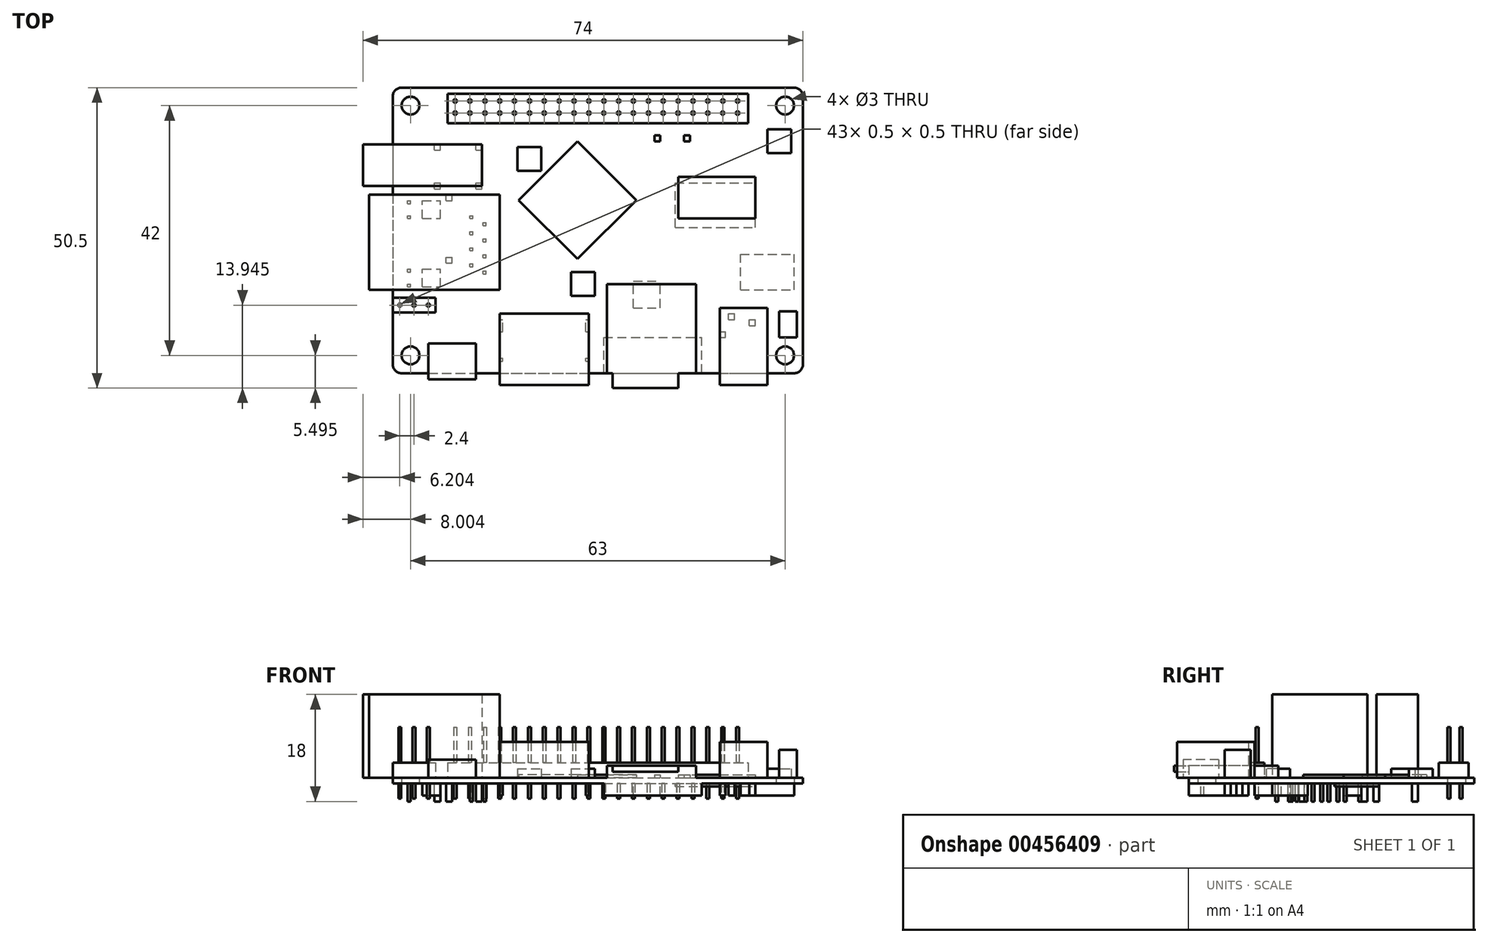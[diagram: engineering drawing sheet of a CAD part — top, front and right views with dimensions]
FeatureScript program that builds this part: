
annotation { "Feature Type Name" : "Feature", "Feature Type Description" : "" }
export const myFeature = defineFeature(function(context is Context, id is Id, definition is map)
    precondition{}
    {
        {
            var Q0;
            Q0=qCreatedBy(makeId("Top.planeOp"),FACE);
            var sketch = newSketch(context, id + "F0", { "sketchPlane" : qUnion([Q0])});
            skLineSegment(sketch, "E0.bottom", {"start": v(-42.34, 28.44) * mm, "end": v(23.66, 28.44) * mm});
            skLineSegment(sketch, "E0.top", {"start": v(-42.34, -19.56) * mm, "end": v(23.66, -19.56) * mm});
            skLineSegment(sketch, "E0.left", {"start": v(-43.84, 26.94) * mm, "end": v(-43.84, -18.06) * mm});
            skLineSegment(sketch, "E0.right", {"start": v(25.16, 26.94) * mm, "end": v(25.16, -18.06) * mm});
            skPoint(sketch, "E1", {"position": v(-43.84, 28.44) * mm});
            skCircle(sketch, "E2", {"center": v(-40.84, 25.44) * mm, "radius": 1.5 * mm});
            skCircle(sketch, "E3", {"center": v(22.16, 25.44) * mm, "radius": 1.5 * mm});
            skCircle(sketch, "E4", {"center": v(22.16, -16.56) * mm, "radius": 1.5 * mm});
            skCircle(sketch, "E5", {"center": v(-40.84, -16.56) * mm, "radius": 1.5 * mm});
            skLineSegment(sketch, "E6.bottom", {"start": v(-37.84, -19.56) * mm, "end": v(19.16, -19.56) * mm});
            skPoint(sketch, "E7.visualSharp", {"position": v(25.16, 28.44) * mm});
            skArc(sketch, "E7.filletArc", {"start": v(25.16, 26.94) * mm, "mid": v(24.72, 28) * mm, "end": v(23.66, 28.44) * mm});
            skArc(sketch, "E8.filletArc", {"start": v(-42.34, 28.44) * mm, "mid": v(-43.4, 28) * mm, "end": v(-43.84, 26.94) * mm});
            skPoint(sketch, "E9.visualSharp", {"position": v(-43.84, -19.56) * mm});
            skArc(sketch, "E9.filletArc", {"start": v(-43.84, -18.06) * mm, "mid": v(-43.4, -19.13) * mm, "end": v(-42.34, -19.56) * mm});
            skPoint(sketch, "E10.visualSharp", {"position": v(25.16, -19.56) * mm});
            skArc(sketch, "E10.filletArc", {"start": v(23.66, -19.56) * mm, "mid": v(24.72, -19.13) * mm, "end": v(25.16, -18.06) * mm});
            skSolve(sketch);
        }
        {
            var Q0;
            Q0=makeQuery(id+"F0.imprint","IMPRINT",FACE,{"disambiguationData":[TD([[makeQuery(id+"F0.imprint","IMPRINT",EDGE,{"derivedFrom":sQuery(id+"F0.wireOp",EDGE,"E0.bottom")}),-1.0]])]});
            extrude(context, id + "F1", {"entities" : qUnion([Q0]), "depth" : 1 * mm});
        }
        {
            var Q0;
            Q0=makeQuery(id+"F1.opExtrude","CAP_FACE",FACE,{"disambiguationData":[OSD([sQuery(id+"F0.wireOp",EDGE,"E0.bottom"),sQuery(id+"F0.wireOp",EDGE,"E0.top"),sQuery(id+"F0.wireOp",EDGE,"E0.left"),sQuery(id+"F0.wireOp",EDGE,"E0.right"),sQuery(id+"F0.wireOp",EDGE,"E2"),sQuery(id+"F0.wireOp",EDGE,"E3"),sQuery(id+"F0.wireOp",EDGE,"E4"),sQuery(id+"F0.wireOp",EDGE,"E5"),sQuery(id+"F0.wireOp",EDGE,"E6.bottom"),sQuery(id+"F0.wireOp",EDGE,"E7.filletArc"),sQuery(id+"F0.wireOp",EDGE,"E8.filletArc"),sQuery(id+"F0.wireOp",EDGE,"E9.filletArc"),sQuery(id+"F0.wireOp",EDGE,"E10.filletArc")])],"isStart":false});
            var sketch = newSketch(context, id + "F2", { "sketchPlane" : qUnion([Q0])});
            skLineSegment(sketch, "E11.bottom", {"start": v(24.16, -13.56) * mm, "end": v(21.16, -13.56) * mm});
            skLineSegment(sketch, "E11.top", {"start": v(24.16, -9.16) * mm, "end": v(21.16, -9.16) * mm});
            skLineSegment(sketch, "E11.left", {"start": v(24.16, -13.56) * mm, "end": v(24.16, -9.16) * mm});
            skLineSegment(sketch, "E11.right", {"start": v(21.16, -13.56) * mm, "end": v(21.16, -9.16) * mm});
            skSolve(sketch);
        }
        {
            var Q0;
            Q0=makeQuery(id+"F2.imprint","IMPRINT",FACE,{"disambiguationData":[TD([[makeQuery(id+"F2.imprint","IMPRINT",EDGE,{"derivedFrom":sQuery(id+"F2.wireOp",EDGE,"E11.bottom")}),-1.0]])]});
            extrude(context, id + "F3", {"entities" : qUnion([Q0]), "operationType" : NewBodyOperationType.ADD, "depth" : 4.7 * mm});
        }
        {
            var Q0;
            Q0=makeQuery(id+"F3.opExtrude","SWEPT_FACE",FACE,{"disambiguationData":[OSD([sQuery(id+"F2.wireOp",EDGE,"E11.left")])]});
            var sketch = newSketch(context, id + "F4", { "sketchPlane" : qUnion([Q0])});
            skCircle(sketch, "E12", {"center": v(-11.39, 3.44) * mm, "radius": 1.05 * mm});
            skSolve(sketch);
        }
        {
            var Q0;
            Q0=sQuery(id+"F4.wireOp",EDGE,"E12");
            extrude(context, id + "F5", {"bodyType" : ToolBodyType.SURFACE, "surfaceEntities" : qUnion([Q0]), "depth" : 2 * mm});
        }
        {
            var Q0;
            Q0=makeQuery(id+"F1.opExtrude","CAP_FACE",FACE,{"disambiguationData":[OSD([sQuery(id+"F0.wireOp",EDGE,"E0.bottom"),sQuery(id+"F0.wireOp",EDGE,"E0.top"),sQuery(id+"F0.wireOp",EDGE,"E0.left"),sQuery(id+"F0.wireOp",EDGE,"E0.right"),sQuery(id+"F0.wireOp",EDGE,"E2"),sQuery(id+"F0.wireOp",EDGE,"E3"),sQuery(id+"F0.wireOp",EDGE,"E4"),sQuery(id+"F0.wireOp",EDGE,"E5"),sQuery(id+"F0.wireOp",EDGE,"E6.bottom"),sQuery(id+"F0.wireOp",EDGE,"E7.filletArc"),sQuery(id+"F0.wireOp",EDGE,"E8.filletArc"),sQuery(id+"F0.wireOp",EDGE,"E9.filletArc"),sQuery(id+"F0.wireOp",EDGE,"E10.filletArc")])],"isStart":false});
            var sketch = newSketch(context, id + "F6", { "sketchPlane" : qUnion([Q0])});
            skLineSegment(sketch, "E13.bottom", {"start": v(11.16, -8.56) * mm, "end": v(19.16, -8.56) * mm});
            skLineSegment(sketch, "E13.top", {"start": v(11.16, -21.56) * mm, "end": v(19.16, -21.56) * mm});
            skLineSegment(sketch, "E13.left", {"start": v(11.16, -8.56) * mm, "end": v(11.16, -21.56) * mm});
            skLineSegment(sketch, "E13.right", {"start": v(19.16, -8.56) * mm, "end": v(19.16, -21.56) * mm});
            skSolve(sketch);
        }
        {
            var Q0;
            Q0 = qSketchRegion(id + "F6", true);
            extrude(context, id + "F7", {"entities" : qUnion([Q0]), "operationType" : NewBodyOperationType.ADD, "depth" : 6 * mm});
        }
        {
            var Q0;
            Q0=makeQuery(id+"F1.opExtrude","CAP_FACE",FACE,{"disambiguationData":[OSD([sQuery(id+"F0.wireOp",EDGE,"E0.bottom"),sQuery(id+"F0.wireOp",EDGE,"E0.top"),sQuery(id+"F0.wireOp",EDGE,"E0.left"),sQuery(id+"F0.wireOp",EDGE,"E0.right"),sQuery(id+"F0.wireOp",EDGE,"E2"),sQuery(id+"F0.wireOp",EDGE,"E3"),sQuery(id+"F0.wireOp",EDGE,"E4"),sQuery(id+"F0.wireOp",EDGE,"E5"),sQuery(id+"F0.wireOp",EDGE,"E6.bottom"),sQuery(id+"F0.wireOp",EDGE,"E7.filletArc"),sQuery(id+"F0.wireOp",EDGE,"E8.filletArc"),sQuery(id+"F0.wireOp",EDGE,"E9.filletArc"),sQuery(id+"F0.wireOp",EDGE,"E10.filletArc")])],"isStart":false});
            var sketch = newSketch(context, id + "F8", { "sketchPlane" : qUnion([Q0])});
            skLineSegment(sketch, "E14.bottom", {"start": v(-7.84, -4.56) * mm, "end": v(7.16, -4.56) * mm});
            skLineSegment(sketch, "E14.top", {"start": v(-7.84, -19.56) * mm, "end": v(7.16, -19.56) * mm});
            skLineSegment(sketch, "E14.left", {"start": v(-7.84, -4.56) * mm, "end": v(-7.84, -19.56) * mm});
            skLineSegment(sketch, "E14.right", {"start": v(7.16, -4.56) * mm, "end": v(7.16, -19.56) * mm});
            skSolve(sketch);
        }
        {
            var Q0;
            Q0 = qSketchRegion(id + "F8", true);
            extrude(context, id + "F9", {"entities" : qUnion([Q0]), "operationType" : NewBodyOperationType.ADD, "depth" : 2 * mm});
        }
        {
            var Q0;
            Q0=makeQuery(id+"F9.boolean.opBoolean","MERGE",FACE,{"derivedFrom":[makeQuery(id+"F1.opExtrude","SWEPT_FACE",FACE,{"disambiguationData":[OSD([sQuery(id+"F0.wireOp",EDGE,"E0.top"),sQuery(id+"F0.wireOp",EDGE,"E6.bottom")])]}),makeQuery(id+"F9.opExtrude","SWEPT_FACE",FACE,{"disambiguationData":[OSD([sQuery(id+"F8.wireOp",EDGE,"E14.top")])]})]});
            var sketch = newSketch(context, id + "F10", { "sketchPlane" : qUnion([Q0])});
            skLineSegment(sketch, "E15.bottom", {"start": v(-6.84, 3) * mm, "end": v(4.16, 3) * mm});
            skLineSegment(sketch, "E15.top", {"start": v(-6.84, 2) * mm, "end": v(4.16, 2) * mm});
            skLineSegment(sketch, "E15.left", {"start": v(-6.84, 3) * mm, "end": v(-6.84, 2) * mm});
            skLineSegment(sketch, "E15.right", {"start": v(4.16, 3) * mm, "end": v(4.16, 2) * mm});
            skSolve(sketch);
        }
        {
            var Q0;
            Q0 = qSketchRegion(id + "F10", true);
            extrude(context, id + "F11", {"entities" : qUnion([Q0]), "operationType" : NewBodyOperationType.ADD, "depth" : 2.5 * mm});
        }
        {
            var Q0;
            Q0=makeQuery(id+"F1.opExtrude","CAP_FACE",FACE,{"disambiguationData":[OSD([sQuery(id+"F0.wireOp",EDGE,"E0.bottom"),sQuery(id+"F0.wireOp",EDGE,"E0.top"),sQuery(id+"F0.wireOp",EDGE,"E0.left"),sQuery(id+"F0.wireOp",EDGE,"E0.right"),sQuery(id+"F0.wireOp",EDGE,"E2"),sQuery(id+"F0.wireOp",EDGE,"E3"),sQuery(id+"F0.wireOp",EDGE,"E4"),sQuery(id+"F0.wireOp",EDGE,"E5"),sQuery(id+"F0.wireOp",EDGE,"E6.bottom"),sQuery(id+"F0.wireOp",EDGE,"E7.filletArc"),sQuery(id+"F0.wireOp",EDGE,"E8.filletArc"),sQuery(id+"F0.wireOp",EDGE,"E9.filletArc"),sQuery(id+"F0.wireOp",EDGE,"E10.filletArc")])],"isStart":false});
            var sketch = newSketch(context, id + "F12", { "sketchPlane" : qUnion([Q0])});
            skLineSegment(sketch, "E16.bottom", {"start": v(-25.84, -9.56) * mm, "end": v(-10.84, -9.56) * mm});
            skLineSegment(sketch, "E16.top", {"start": v(-25.84, -21.56) * mm, "end": v(-10.84, -21.56) * mm});
            skLineSegment(sketch, "E16.left", {"start": v(-25.84, -9.56) * mm, "end": v(-25.84, -21.56) * mm});
            skLineSegment(sketch, "E16.right", {"start": v(-10.84, -9.56) * mm, "end": v(-10.84, -21.56) * mm});
            skSolve(sketch);
        }
        {
            var Q0;
            Q0 = qSketchRegion(id + "F12", true);
            extrude(context, id + "F13", {"entities" : qUnion([Q0]), "operationType" : NewBodyOperationType.ADD, "depth" : 6 * mm});
        }
        {
            var Q0;
            Q0=makeQuery(id+"F1.opExtrude","CAP_FACE",FACE,{"disambiguationData":[OSD([sQuery(id+"F0.wireOp",EDGE,"E0.bottom"),sQuery(id+"F0.wireOp",EDGE,"E0.top"),sQuery(id+"F0.wireOp",EDGE,"E0.left"),sQuery(id+"F0.wireOp",EDGE,"E0.right"),sQuery(id+"F0.wireOp",EDGE,"E2"),sQuery(id+"F0.wireOp",EDGE,"E3"),sQuery(id+"F0.wireOp",EDGE,"E4"),sQuery(id+"F0.wireOp",EDGE,"E5"),sQuery(id+"F0.wireOp",EDGE,"E6.bottom"),sQuery(id+"F0.wireOp",EDGE,"E7.filletArc"),sQuery(id+"F0.wireOp",EDGE,"E8.filletArc"),sQuery(id+"F0.wireOp",EDGE,"E9.filletArc"),sQuery(id+"F0.wireOp",EDGE,"E10.filletArc")])],"isStart":false});
            var sketch = newSketch(context, id + "F14", { "sketchPlane" : qUnion([Q0])});
            skLineSegment(sketch, "E17.bottom", {"start": v(-37.84, -14.56) * mm, "end": v(-29.84, -14.56) * mm});
            skLineSegment(sketch, "E17.top", {"start": v(-37.84, -20.56) * mm, "end": v(-29.84, -20.56) * mm});
            skLineSegment(sketch, "E17.left", {"start": v(-37.84, -14.56) * mm, "end": v(-37.84, -20.56) * mm});
            skLineSegment(sketch, "E17.right", {"start": v(-29.84, -14.56) * mm, "end": v(-29.84, -20.56) * mm});
            skSolve(sketch);
        }
        {
            var Q0;
            Q0 = qSketchRegion(id + "F14", true);
            extrude(context, id + "F15", {"entities" : qUnion([Q0]), "operationType" : NewBodyOperationType.ADD, "depth" : 3 * mm});
        }
        {
            var Q0;
            Q0=makeQuery(id+"F1.opExtrude","CAP_FACE",FACE,{"disambiguationData":[OSD([sQuery(id+"F0.wireOp",EDGE,"E0.bottom"),sQuery(id+"F0.wireOp",EDGE,"E0.top"),sQuery(id+"F0.wireOp",EDGE,"E0.left"),sQuery(id+"F0.wireOp",EDGE,"E0.right"),sQuery(id+"F0.wireOp",EDGE,"E2"),sQuery(id+"F0.wireOp",EDGE,"E3"),sQuery(id+"F0.wireOp",EDGE,"E4"),sQuery(id+"F0.wireOp",EDGE,"E5"),sQuery(id+"F0.wireOp",EDGE,"E6.bottom"),sQuery(id+"F0.wireOp",EDGE,"E7.filletArc"),sQuery(id+"F0.wireOp",EDGE,"E8.filletArc"),sQuery(id+"F0.wireOp",EDGE,"E9.filletArc"),sQuery(id+"F0.wireOp",EDGE,"E10.filletArc")])],"isStart":false});
            var sketch = newSketch(context, id + "F16", { "sketchPlane" : qUnion([Q0])});
            skLineSegment(sketch, "E18.bottom", {"start": v(-43.84, -6.86) * mm, "end": v(-36.64, -6.86) * mm});
            skLineSegment(sketch, "E18.top", {"start": v(-43.84, -9.36) * mm, "end": v(-36.64, -9.36) * mm});
            skLineSegment(sketch, "E18.left", {"start": v(-43.84, -6.86) * mm, "end": v(-43.84, -9.36) * mm});
            skLineSegment(sketch, "E18.right", {"start": v(-36.64, -6.86) * mm, "end": v(-36.64, -9.36) * mm});
            skSolve(sketch);
        }
        {
            var Q0;
            Q0 = qSketchRegion(id + "F16", true);
            extrude(context, id + "F17", {"entities" : qUnion([Q0]), "operationType" : NewBodyOperationType.ADD, "depth" : 2.5 * mm});
        }
        {
            var Q0;
            Q0=makeQuery(id+"F17.opExtrude","CAP_FACE",FACE,{"disambiguationData":[OSD([sQuery(id+"F16.wireOp",EDGE,"E18.bottom"),sQuery(id+"F16.wireOp",EDGE,"E18.top"),sQuery(id+"F16.wireOp",EDGE,"E18.left"),sQuery(id+"F16.wireOp",EDGE,"E18.right")])],"isStart":false});
            var sketch = newSketch(context, id + "F18", { "sketchPlane" : qUnion([Q0])});
            skLineSegment(sketch, "E19.bottom", {"start": v(-42.89, -7.86) * mm, "end": v(-42.39, -7.86) * mm});
            skLineSegment(sketch, "E19.top", {"start": v(-42.89, -8.36) * mm, "end": v(-42.39, -8.36) * mm});
            skLineSegment(sketch, "E19.left", {"start": v(-42.89, -7.86) * mm, "end": v(-42.89, -8.36) * mm});
            skLineSegment(sketch, "E19.right", {"start": v(-42.39, -7.86) * mm, "end": v(-42.39, -8.36) * mm});
            skLineSegment(sketch, "E20.bottom", {"start": v(-40.49, -7.86) * mm, "end": v(-39.99, -7.86) * mm});
            skLineSegment(sketch, "E20.top", {"start": v(-40.49, -8.36) * mm, "end": v(-39.99, -8.36) * mm});
            skLineSegment(sketch, "E20.left", {"start": v(-40.49, -7.86) * mm, "end": v(-40.49, -8.36) * mm});
            skLineSegment(sketch, "E20.right", {"start": v(-39.99, -7.86) * mm, "end": v(-39.99, -8.36) * mm});
            skLineSegment(sketch, "E21.bottom", {"start": v(-38.09, -7.86) * mm, "end": v(-37.59, -7.86) * mm});
            skLineSegment(sketch, "E21.top", {"start": v(-38.09, -8.36) * mm, "end": v(-37.59, -8.36) * mm});
            skLineSegment(sketch, "E21.left", {"start": v(-38.09, -7.86) * mm, "end": v(-38.09, -8.36) * mm});
            skLineSegment(sketch, "E21.right", {"start": v(-37.59, -7.86) * mm, "end": v(-37.59, -8.36) * mm});
            skSolve(sketch);
        }
        {
            var Q0;
            Q0 = qSketchRegion(id + "F18", true);
            extrude(context, id + "F19", {"entities" : qUnion([Q0]), "operationType" : NewBodyOperationType.ADD, "depth" : 6 * mm});
        }
        {
            var Q0;
            Q0=makeQuery(id+"F1.opExtrude","CAP_FACE",FACE,{"disambiguationData":[OSD([sQuery(id+"F0.wireOp",EDGE,"E0.bottom"),sQuery(id+"F0.wireOp",EDGE,"E0.top"),sQuery(id+"F0.wireOp",EDGE,"E0.left"),sQuery(id+"F0.wireOp",EDGE,"E0.right"),sQuery(id+"F0.wireOp",EDGE,"E2"),sQuery(id+"F0.wireOp",EDGE,"E3"),sQuery(id+"F0.wireOp",EDGE,"E4"),sQuery(id+"F0.wireOp",EDGE,"E5"),sQuery(id+"F0.wireOp",EDGE,"E6.bottom"),sQuery(id+"F0.wireOp",EDGE,"E7.filletArc"),sQuery(id+"F0.wireOp",EDGE,"E8.filletArc"),sQuery(id+"F0.wireOp",EDGE,"E9.filletArc"),sQuery(id+"F0.wireOp",EDGE,"E10.filletArc")])],"isStart":false});
            var sketch = newSketch(context, id + "F20", { "sketchPlane" : qUnion([Q0])});
            skLineSegment(sketch, "E22.bottom", {"start": v(-25.84, 10.44) * mm, "end": v(-47.84, 10.44) * mm});
            skLineSegment(sketch, "E22.top", {"start": v(-25.84, -5.56) * mm, "end": v(-47.84, -5.56) * mm});
            skLineSegment(sketch, "E22.left", {"start": v(-25.84, 10.44) * mm, "end": v(-25.84, -5.56) * mm});
            skLineSegment(sketch, "E22.right", {"start": v(-47.84, 10.44) * mm, "end": v(-47.84, -5.56) * mm});
            skSolve(sketch);
        }
        {
            var Q0;
            Q0 = qSketchRegion(id + "F20", true);
            extrude(context, id + "F21", {"entities" : qUnion([Q0]), "operationType" : NewBodyOperationType.ADD, "depth" : 14 * mm});
        }
        {
            var Q0;
            Q0=makeQuery(id+"F1.opExtrude","CAP_FACE",FACE,{"disambiguationData":[OSD([sQuery(id+"F0.wireOp",EDGE,"E0.bottom"),sQuery(id+"F0.wireOp",EDGE,"E0.top"),sQuery(id+"F0.wireOp",EDGE,"E0.left"),sQuery(id+"F0.wireOp",EDGE,"E0.right"),sQuery(id+"F0.wireOp",EDGE,"E2"),sQuery(id+"F0.wireOp",EDGE,"E3"),sQuery(id+"F0.wireOp",EDGE,"E4"),sQuery(id+"F0.wireOp",EDGE,"E5"),sQuery(id+"F0.wireOp",EDGE,"E6.bottom"),sQuery(id+"F0.wireOp",EDGE,"E7.filletArc"),sQuery(id+"F0.wireOp",EDGE,"E8.filletArc"),sQuery(id+"F0.wireOp",EDGE,"E9.filletArc"),sQuery(id+"F0.wireOp",EDGE,"E10.filletArc")])],"isStart":false});
            var sketch = newSketch(context, id + "F22", { "sketchPlane" : qUnion([Q0])});
            skLineSegment(sketch, "E23.bottom", {"start": v(-48.84, 18.94) * mm, "end": v(-28.84, 18.94) * mm});
            skLineSegment(sketch, "E23.top", {"start": v(-48.84, 11.94) * mm, "end": v(-28.84, 11.94) * mm});
            skLineSegment(sketch, "E23.left", {"start": v(-48.84, 18.94) * mm, "end": v(-48.84, 11.94) * mm});
            skLineSegment(sketch, "E23.right", {"start": v(-28.84, 18.94) * mm, "end": v(-28.84, 11.94) * mm});
            skSolve(sketch);
        }
        {
            var Q0;
            Q0 = qSketchRegion(id + "F22", true);
            extrude(context, id + "F23", {"entities" : qUnion([Q0]), "operationType" : NewBodyOperationType.ADD, "depth" : 14 * mm});
        }
        {
            var Q0;
            Q0=makeQuery(id+"F1.opExtrude","CAP_FACE",FACE,{"disambiguationData":[OSD([sQuery(id+"F0.wireOp",EDGE,"E0.bottom"),sQuery(id+"F0.wireOp",EDGE,"E0.top"),sQuery(id+"F0.wireOp",EDGE,"E0.left"),sQuery(id+"F0.wireOp",EDGE,"E0.right"),sQuery(id+"F0.wireOp",EDGE,"E2"),sQuery(id+"F0.wireOp",EDGE,"E3"),sQuery(id+"F0.wireOp",EDGE,"E4"),sQuery(id+"F0.wireOp",EDGE,"E5"),sQuery(id+"F0.wireOp",EDGE,"E6.bottom"),sQuery(id+"F0.wireOp",EDGE,"E7.filletArc"),sQuery(id+"F0.wireOp",EDGE,"E8.filletArc"),sQuery(id+"F0.wireOp",EDGE,"E9.filletArc"),sQuery(id+"F0.wireOp",EDGE,"E10.filletArc")])],"isStart":false});
            var sketch = newSketch(context, id + "F24", { "sketchPlane" : qUnion([Q0])});
            skLineSegment(sketch, "E24.bottom", {"start": v(-34.59, 27.44) * mm, "end": v(15.91, 27.44) * mm});
            skLineSegment(sketch, "E24.top", {"start": v(-34.59, 22.44) * mm, "end": v(15.91, 22.44) * mm});
            skLineSegment(sketch, "E24.left", {"start": v(-34.59, 27.44) * mm, "end": v(-34.59, 22.44) * mm});
            skLineSegment(sketch, "E24.right", {"start": v(15.91, 27.44) * mm, "end": v(15.91, 22.44) * mm});
            skSolve(sketch);
        }
        {
            var Q0;
            Q0 = qSketchRegion(id + "F24", true);
            extrude(context, id + "F25", {"entities" : qUnion([Q0]), "operationType" : NewBodyOperationType.ADD, "depth" : 2.5 * mm});
        }
        {
            var Q0;
            Q0=makeQuery(id+"F25.opExtrude","CAP_FACE",FACE,{"disambiguationData":[OSD([sQuery(id+"F24.wireOp",EDGE,"E24.bottom"),sQuery(id+"F24.wireOp",EDGE,"E24.top"),sQuery(id+"F24.wireOp",EDGE,"E24.left"),sQuery(id+"F24.wireOp",EDGE,"E24.right")])],"isStart":false});
            var sketch = newSketch(context, id + "F26", { "sketchPlane" : qUnion([Q0])});
            skLineSegment(sketch, "E25.bottom", {"start": v(-33.59, 26.44) * mm, "end": v(-33.09, 26.44) * mm});
            skLineSegment(sketch, "E25.top", {"start": v(-33.59, 25.94) * mm, "end": v(-33.09, 25.94) * mm});
            skLineSegment(sketch, "E25.left", {"start": v(-33.59, 26.44) * mm, "end": v(-33.59, 25.94) * mm});
            skLineSegment(sketch, "E25.right", {"start": v(-33.09, 26.44) * mm, "end": v(-33.09, 25.94) * mm});
            skLineSegment(sketch, "E26.1.0.0", {"start": v(-31.09, 26.44) * mm, "end": v(-31.09, 25.94) * mm});
            skLineSegment(sketch, "E26.1.0.1", {"start": v(-31.09, 26.44) * mm, "end": v(-30.59, 26.44) * mm});
            skLineSegment(sketch, "E26.1.0.2", {"start": v(-30.59, 26.44) * mm, "end": v(-30.59, 25.94) * mm});
            skLineSegment(sketch, "E26.1.0.3", {"start": v(-31.09, 25.94) * mm, "end": v(-30.59, 25.94) * mm});
            skLineSegment(sketch, "E26.2.0.0", {"start": v(-28.59, 26.44) * mm, "end": v(-28.59, 25.94) * mm});
            skLineSegment(sketch, "E26.2.0.1", {"start": v(-28.59, 26.44) * mm, "end": v(-28.09, 26.44) * mm});
            skLineSegment(sketch, "E26.2.0.2", {"start": v(-28.09, 26.44) * mm, "end": v(-28.09, 25.94) * mm});
            skLineSegment(sketch, "E26.2.0.3", {"start": v(-28.59, 25.94) * mm, "end": v(-28.09, 25.94) * mm});
            skLineSegment(sketch, "E26.direction1", {"start": v(-33.59, 25.94) * mm, "end": v(-31.09, 25.94) * mm, "construction": true});
            skLineSegment(sketch, "E27.0.3.0", {"start": v(-26.09, 26.44) * mm, "end": v(-26.09, 25.94) * mm});
            skLineSegment(sketch, "E27.3.3.0", {"start": v(-26.09, 26.44) * mm, "end": v(-25.59, 26.44) * mm});
            skLineSegment(sketch, "E27.6.3.0", {"start": v(-25.59, 26.44) * mm, "end": v(-25.59, 25.94) * mm});
            skLineSegment(sketch, "E27.9.3.0", {"start": v(-26.09, 25.94) * mm, "end": v(-25.59, 25.94) * mm});
            skLineSegment(sketch, "E27.0.4.0", {"start": v(-23.59, 26.44) * mm, "end": v(-23.59, 25.94) * mm});
            skLineSegment(sketch, "E27.3.4.0", {"start": v(-23.59, 26.44) * mm, "end": v(-23.09, 26.44) * mm});
            skLineSegment(sketch, "E27.6.4.0", {"start": v(-23.09, 26.44) * mm, "end": v(-23.09, 25.94) * mm});
            skLineSegment(sketch, "E27.9.4.0", {"start": v(-23.59, 25.94) * mm, "end": v(-23.09, 25.94) * mm});
            skLineSegment(sketch, "E27.0.5.0", {"start": v(-21.09, 26.44) * mm, "end": v(-21.09, 25.94) * mm});
            skLineSegment(sketch, "E27.3.5.0", {"start": v(-21.09, 26.44) * mm, "end": v(-20.59, 26.44) * mm});
            skLineSegment(sketch, "E27.6.5.0", {"start": v(-20.59, 26.44) * mm, "end": v(-20.59, 25.94) * mm});
            skLineSegment(sketch, "E27.9.5.0", {"start": v(-21.09, 25.94) * mm, "end": v(-20.59, 25.94) * mm});
            skLineSegment(sketch, "E27.0.6.0", {"start": v(-18.59, 26.44) * mm, "end": v(-18.59, 25.94) * mm});
            skLineSegment(sketch, "E27.3.6.0", {"start": v(-18.59, 26.44) * mm, "end": v(-18.09, 26.44) * mm});
            skLineSegment(sketch, "E27.6.6.0", {"start": v(-18.09, 26.44) * mm, "end": v(-18.09, 25.94) * mm});
            skLineSegment(sketch, "E27.9.6.0", {"start": v(-18.59, 25.94) * mm, "end": v(-18.09, 25.94) * mm});
            skLineSegment(sketch, "E27.0.7.0", {"start": v(-16.09, 26.44) * mm, "end": v(-16.09, 25.94) * mm});
            skLineSegment(sketch, "E27.3.7.0", {"start": v(-16.09, 26.44) * mm, "end": v(-15.59, 26.44) * mm});
            skLineSegment(sketch, "E27.6.7.0", {"start": v(-15.59, 26.44) * mm, "end": v(-15.59, 25.94) * mm});
            skLineSegment(sketch, "E27.9.7.0", {"start": v(-16.09, 25.94) * mm, "end": v(-15.59, 25.94) * mm});
            skLineSegment(sketch, "E27.0.8.0", {"start": v(-13.59, 26.44) * mm, "end": v(-13.59, 25.94) * mm});
            skLineSegment(sketch, "E27.3.8.0", {"start": v(-13.59, 26.44) * mm, "end": v(-13.09, 26.44) * mm});
            skLineSegment(sketch, "E27.6.8.0", {"start": v(-13.09, 26.44) * mm, "end": v(-13.09, 25.94) * mm});
            skLineSegment(sketch, "E27.9.8.0", {"start": v(-13.59, 25.94) * mm, "end": v(-13.09, 25.94) * mm});
            skLineSegment(sketch, "E27.0.9.0", {"start": v(-11.09, 26.44) * mm, "end": v(-11.09, 25.94) * mm});
            skLineSegment(sketch, "E27.3.9.0", {"start": v(-11.09, 26.44) * mm, "end": v(-10.59, 26.44) * mm});
            skLineSegment(sketch, "E27.6.9.0", {"start": v(-10.59, 26.44) * mm, "end": v(-10.59, 25.94) * mm});
            skLineSegment(sketch, "E27.9.9.0", {"start": v(-11.09, 25.94) * mm, "end": v(-10.59, 25.94) * mm});
            skLineSegment(sketch, "E27.0.10.0", {"start": v(-8.59, 26.44) * mm, "end": v(-8.59, 25.94) * mm});
            skLineSegment(sketch, "E27.3.10.0", {"start": v(-8.59, 26.44) * mm, "end": v(-8.09, 26.44) * mm});
            skLineSegment(sketch, "E27.6.10.0", {"start": v(-8.09, 26.44) * mm, "end": v(-8.09, 25.94) * mm});
            skLineSegment(sketch, "E27.9.10.0", {"start": v(-8.59, 25.94) * mm, "end": v(-8.09, 25.94) * mm});
            skLineSegment(sketch, "E27.0.11.0", {"start": v(-6.09, 26.44) * mm, "end": v(-6.09, 25.94) * mm});
            skLineSegment(sketch, "E27.3.11.0", {"start": v(-6.09, 26.44) * mm, "end": v(-5.59, 26.44) * mm});
            skLineSegment(sketch, "E27.6.11.0", {"start": v(-5.59, 26.44) * mm, "end": v(-5.59, 25.94) * mm});
            skLineSegment(sketch, "E27.9.11.0", {"start": v(-6.09, 25.94) * mm, "end": v(-5.59, 25.94) * mm});
            skLineSegment(sketch, "E27.0.12.0", {"start": v(-3.59, 26.44) * mm, "end": v(-3.59, 25.94) * mm});
            skLineSegment(sketch, "E27.3.12.0", {"start": v(-3.59, 26.44) * mm, "end": v(-3.09, 26.44) * mm});
            skLineSegment(sketch, "E27.6.12.0", {"start": v(-3.09, 26.44) * mm, "end": v(-3.09, 25.94) * mm});
            skLineSegment(sketch, "E27.9.12.0", {"start": v(-3.59, 25.94) * mm, "end": v(-3.09, 25.94) * mm});
            skLineSegment(sketch, "E27.0.13.0", {"start": v(-1.09, 26.44) * mm, "end": v(-1.09, 25.94) * mm});
            skLineSegment(sketch, "E27.3.13.0", {"start": v(-1.09, 26.44) * mm, "end": v(-0.59, 26.44) * mm});
            skLineSegment(sketch, "E27.6.13.0", {"start": v(-0.59, 26.44) * mm, "end": v(-0.59, 25.94) * mm});
            skLineSegment(sketch, "E27.9.13.0", {"start": v(-1.09, 25.94) * mm, "end": v(-0.59, 25.94) * mm});
            skLineSegment(sketch, "E27.0.14.0", {"start": v(1.41, 26.44) * mm, "end": v(1.41, 25.94) * mm});
            skLineSegment(sketch, "E27.3.14.0", {"start": v(1.41, 26.44) * mm, "end": v(1.91, 26.44) * mm});
            skLineSegment(sketch, "E27.6.14.0", {"start": v(1.91, 26.44) * mm, "end": v(1.91, 25.94) * mm});
            skLineSegment(sketch, "E27.9.14.0", {"start": v(1.41, 25.94) * mm, "end": v(1.91, 25.94) * mm});
            skLineSegment(sketch, "E27.0.15.0", {"start": v(3.91, 26.44) * mm, "end": v(3.91, 25.94) * mm});
            skLineSegment(sketch, "E27.3.15.0", {"start": v(3.91, 26.44) * mm, "end": v(4.41, 26.44) * mm});
            skLineSegment(sketch, "E27.6.15.0", {"start": v(4.41, 26.44) * mm, "end": v(4.41, 25.94) * mm});
            skLineSegment(sketch, "E27.9.15.0", {"start": v(3.91, 25.94) * mm, "end": v(4.41, 25.94) * mm});
            skLineSegment(sketch, "E27.0.16.0", {"start": v(6.41, 26.44) * mm, "end": v(6.41, 25.94) * mm});
            skLineSegment(sketch, "E27.3.16.0", {"start": v(6.41, 26.44) * mm, "end": v(6.91, 26.44) * mm});
            skLineSegment(sketch, "E27.6.16.0", {"start": v(6.91, 26.44) * mm, "end": v(6.91, 25.94) * mm});
            skLineSegment(sketch, "E27.9.16.0", {"start": v(6.41, 25.94) * mm, "end": v(6.91, 25.94) * mm});
            skLineSegment(sketch, "E27.0.17.0", {"start": v(8.91, 26.44) * mm, "end": v(8.91, 25.94) * mm});
            skLineSegment(sketch, "E27.3.17.0", {"start": v(8.91, 26.44) * mm, "end": v(9.41, 26.44) * mm});
            skLineSegment(sketch, "E27.6.17.0", {"start": v(9.41, 26.44) * mm, "end": v(9.41, 25.94) * mm});
            skLineSegment(sketch, "E27.9.17.0", {"start": v(8.91, 25.94) * mm, "end": v(9.41, 25.94) * mm});
            skLineSegment(sketch, "E27.0.18.0", {"start": v(11.41, 26.44) * mm, "end": v(11.41, 25.94) * mm});
            skLineSegment(sketch, "E27.3.18.0", {"start": v(11.41, 26.44) * mm, "end": v(11.91, 26.44) * mm});
            skLineSegment(sketch, "E27.6.18.0", {"start": v(11.91, 26.44) * mm, "end": v(11.91, 25.94) * mm});
            skLineSegment(sketch, "E27.9.18.0", {"start": v(11.41, 25.94) * mm, "end": v(11.91, 25.94) * mm});
            skLineSegment(sketch, "E27.0.19.0", {"start": v(13.91, 26.44) * mm, "end": v(13.91, 25.94) * mm});
            skLineSegment(sketch, "E27.3.19.0", {"start": v(13.91, 26.44) * mm, "end": v(14.41, 26.44) * mm});
            skLineSegment(sketch, "E27.6.19.0", {"start": v(14.41, 26.44) * mm, "end": v(14.41, 25.94) * mm});
            skLineSegment(sketch, "E27.9.19.0", {"start": v(13.91, 25.94) * mm, "end": v(14.41, 25.94) * mm});
            skLineSegment(sketch, "E28.direction1", {"start": v(13.91, 25.94) * mm, "end": v(13.9, 23.94) * mm, "construction": true});
            skLineSegment(sketch, "E29.0.1.0", {"start": v(13.9, 23.94) * mm, "end": v(14.4, 23.94) * mm});
            skLineSegment(sketch, "E29.3.1.0", {"start": v(14.4, 24.44) * mm, "end": v(14.4, 23.94) * mm});
            skLineSegment(sketch, "E29.6.1.0", {"start": v(13.9, 24.44) * mm, "end": v(14.4, 24.44) * mm});
            skLineSegment(sketch, "E29.9.1.0", {"start": v(13.9, 24.44) * mm, "end": v(13.9, 23.94) * mm});
            skLineSegment(sketch, "E30.1.0.0", {"start": v(11.4, 23.93) * mm, "end": v(11.9, 23.93) * mm});
            skLineSegment(sketch, "E30.1.0.1", {"start": v(11.41, 25.93) * mm, "end": v(11.4, 23.93) * mm, "construction": true});
            skLineSegment(sketch, "E30.1.0.2", {"start": v(11.9, 24.43) * mm, "end": v(11.9, 23.93) * mm});
            skLineSegment(sketch, "E30.1.0.3", {"start": v(11.4, 24.43) * mm, "end": v(11.9, 24.43) * mm});
            skLineSegment(sketch, "E30.2.0.0", {"start": v(8.9, 23.93) * mm, "end": v(9.4, 23.93) * mm});
            skLineSegment(sketch, "E30.2.0.1", {"start": v(8.91, 25.93) * mm, "end": v(8.9, 23.93) * mm, "construction": true});
            skLineSegment(sketch, "E30.2.0.2", {"start": v(9.4, 24.43) * mm, "end": v(9.4, 23.93) * mm});
            skLineSegment(sketch, "E30.2.0.3", {"start": v(8.9, 24.43) * mm, "end": v(9.4, 24.43) * mm});
            skLineSegment(sketch, "E30.direction1", {"start": v(13.9, 23.94) * mm, "end": v(11.4, 23.93) * mm, "construction": true});
            skLineSegment(sketch, "E31.0.3.0", {"start": v(6.4, 23.93) * mm, "end": v(6.9, 23.93) * mm});
            skLineSegment(sketch, "E31.3.3.0", {"start": v(6.41, 25.93) * mm, "end": v(6.4, 23.93) * mm, "construction": true});
            skLineSegment(sketch, "E31.6.3.0", {"start": v(6.9, 24.43) * mm, "end": v(6.9, 23.93) * mm});
            skLineSegment(sketch, "E31.9.3.0", {"start": v(6.4, 24.43) * mm, "end": v(6.9, 24.43) * mm});
            skLineSegment(sketch, "E31.0.4.0", {"start": v(3.9, 23.93) * mm, "end": v(4.4, 23.93) * mm});
            skLineSegment(sketch, "E31.3.4.0", {"start": v(3.91, 25.93) * mm, "end": v(3.9, 23.93) * mm, "construction": true});
            skLineSegment(sketch, "E31.6.4.0", {"start": v(4.4, 24.43) * mm, "end": v(4.4, 23.93) * mm});
            skLineSegment(sketch, "E31.9.4.0", {"start": v(3.9, 24.43) * mm, "end": v(4.4, 24.43) * mm});
            skLineSegment(sketch, "E31.0.5.0", {"start": v(1.4, 23.93) * mm, "end": v(1.9, 23.93) * mm});
            skLineSegment(sketch, "E31.3.5.0", {"start": v(1.41, 25.93) * mm, "end": v(1.4, 23.93) * mm, "construction": true});
            skLineSegment(sketch, "E31.6.5.0", {"start": v(1.9, 24.43) * mm, "end": v(1.9, 23.93) * mm});
            skLineSegment(sketch, "E31.9.5.0", {"start": v(1.4, 24.43) * mm, "end": v(1.9, 24.43) * mm});
            skLineSegment(sketch, "E31.0.6.0", {"start": v(-1.1, 23.93) * mm, "end": v(-0.6, 23.93) * mm});
            skLineSegment(sketch, "E31.3.6.0", {"start": v(-1.09, 25.93) * mm, "end": v(-1.1, 23.93) * mm, "construction": true});
            skLineSegment(sketch, "E31.6.6.0", {"start": v(-0.6, 24.43) * mm, "end": v(-0.6, 23.93) * mm});
            skLineSegment(sketch, "E31.9.6.0", {"start": v(-1.1, 24.43) * mm, "end": v(-0.6, 24.43) * mm});
            skLineSegment(sketch, "E31.0.7.0", {"start": v(-3.6, 23.93) * mm, "end": v(-3.1, 23.93) * mm});
            skLineSegment(sketch, "E31.3.7.0", {"start": v(-3.59, 25.93) * mm, "end": v(-3.6, 23.93) * mm, "construction": true});
            skLineSegment(sketch, "E31.6.7.0", {"start": v(-3.1, 24.43) * mm, "end": v(-3.1, 23.93) * mm});
            skLineSegment(sketch, "E31.9.7.0", {"start": v(-3.6, 24.43) * mm, "end": v(-3.1, 24.43) * mm});
            skLineSegment(sketch, "E31.0.8.0", {"start": v(-6.1, 23.93) * mm, "end": v(-5.6, 23.93) * mm});
            skLineSegment(sketch, "E31.3.8.0", {"start": v(-6.09, 25.93) * mm, "end": v(-6.1, 23.93) * mm, "construction": true});
            skLineSegment(sketch, "E31.6.8.0", {"start": v(-5.6, 24.43) * mm, "end": v(-5.6, 23.93) * mm});
            skLineSegment(sketch, "E31.9.8.0", {"start": v(-6.1, 24.43) * mm, "end": v(-5.6, 24.43) * mm});
            skLineSegment(sketch, "E31.0.9.0", {"start": v(-8.6, 23.93) * mm, "end": v(-8.1, 23.93) * mm});
            skLineSegment(sketch, "E31.3.9.0", {"start": v(-8.59, 25.93) * mm, "end": v(-8.6, 23.93) * mm, "construction": true});
            skLineSegment(sketch, "E31.6.9.0", {"start": v(-8.1, 24.43) * mm, "end": v(-8.1, 23.93) * mm});
            skLineSegment(sketch, "E31.9.9.0", {"start": v(-8.6, 24.43) * mm, "end": v(-8.1, 24.43) * mm});
            skLineSegment(sketch, "E31.0.10.0", {"start": v(-11.1, 23.93) * mm, "end": v(-10.6, 23.93) * mm});
            skLineSegment(sketch, "E31.3.10.0", {"start": v(-11.09, 25.93) * mm, "end": v(-11.1, 23.93) * mm, "construction": true});
            skLineSegment(sketch, "E31.6.10.0", {"start": v(-10.6, 24.43) * mm, "end": v(-10.6, 23.93) * mm});
            skLineSegment(sketch, "E31.9.10.0", {"start": v(-11.1, 24.43) * mm, "end": v(-10.6, 24.43) * mm});
            skLineSegment(sketch, "E31.0.11.0", {"start": v(-13.6, 23.93) * mm, "end": v(-13.1, 23.93) * mm});
            skLineSegment(sketch, "E31.3.11.0", {"start": v(-13.59, 25.93) * mm, "end": v(-13.6, 23.93) * mm, "construction": true});
            skLineSegment(sketch, "E31.6.11.0", {"start": v(-13.1, 24.43) * mm, "end": v(-13.1, 23.93) * mm});
            skLineSegment(sketch, "E31.9.11.0", {"start": v(-13.6, 24.43) * mm, "end": v(-13.1, 24.43) * mm});
            skLineSegment(sketch, "E31.0.12.0", {"start": v(-16.1, 23.93) * mm, "end": v(-15.6, 23.93) * mm});
            skLineSegment(sketch, "E31.3.12.0", {"start": v(-16.09, 25.93) * mm, "end": v(-16.1, 23.93) * mm, "construction": true});
            skLineSegment(sketch, "E31.6.12.0", {"start": v(-15.6, 24.43) * mm, "end": v(-15.6, 23.93) * mm});
            skLineSegment(sketch, "E31.9.12.0", {"start": v(-16.1, 24.43) * mm, "end": v(-15.6, 24.43) * mm});
            skLineSegment(sketch, "E31.0.13.0", {"start": v(-18.6, 23.93) * mm, "end": v(-18.1, 23.93) * mm});
            skLineSegment(sketch, "E31.3.13.0", {"start": v(-18.59, 25.93) * mm, "end": v(-18.6, 23.93) * mm, "construction": true});
            skLineSegment(sketch, "E31.6.13.0", {"start": v(-18.1, 24.43) * mm, "end": v(-18.1, 23.93) * mm});
            skLineSegment(sketch, "E31.9.13.0", {"start": v(-18.6, 24.43) * mm, "end": v(-18.1, 24.43) * mm});
            skLineSegment(sketch, "E31.0.14.0", {"start": v(-21.1, 23.92) * mm, "end": v(-20.6, 23.92) * mm});
            skLineSegment(sketch, "E31.3.14.0", {"start": v(-21.09, 25.92) * mm, "end": v(-21.1, 23.92) * mm, "construction": true});
            skLineSegment(sketch, "E31.6.14.0", {"start": v(-20.6, 24.42) * mm, "end": v(-20.6, 23.92) * mm});
            skLineSegment(sketch, "E31.9.14.0", {"start": v(-21.1, 24.42) * mm, "end": v(-20.6, 24.42) * mm});
            skLineSegment(sketch, "E31.0.15.0", {"start": v(-23.6, 23.92) * mm, "end": v(-23.1, 23.92) * mm});
            skLineSegment(sketch, "E31.3.15.0", {"start": v(-23.59, 25.92) * mm, "end": v(-23.6, 23.92) * mm, "construction": true});
            skLineSegment(sketch, "E31.6.15.0", {"start": v(-23.1, 24.42) * mm, "end": v(-23.1, 23.92) * mm});
            skLineSegment(sketch, "E31.9.15.0", {"start": v(-23.6, 24.42) * mm, "end": v(-23.1, 24.42) * mm});
            skLineSegment(sketch, "E31.0.16.0", {"start": v(-26.1, 23.92) * mm, "end": v(-25.6, 23.92) * mm});
            skLineSegment(sketch, "E31.3.16.0", {"start": v(-26.09, 25.92) * mm, "end": v(-26.1, 23.92) * mm, "construction": true});
            skLineSegment(sketch, "E31.6.16.0", {"start": v(-25.6, 24.42) * mm, "end": v(-25.6, 23.92) * mm});
            skLineSegment(sketch, "E31.9.16.0", {"start": v(-26.1, 24.42) * mm, "end": v(-25.6, 24.42) * mm});
            skLineSegment(sketch, "E31.0.17.0", {"start": v(-28.6, 23.92) * mm, "end": v(-28.1, 23.92) * mm});
            skLineSegment(sketch, "E31.3.17.0", {"start": v(-28.59, 25.92) * mm, "end": v(-28.6, 23.92) * mm, "construction": true});
            skLineSegment(sketch, "E31.6.17.0", {"start": v(-28.1, 24.42) * mm, "end": v(-28.1, 23.92) * mm});
            skLineSegment(sketch, "E31.9.17.0", {"start": v(-28.6, 24.42) * mm, "end": v(-28.1, 24.42) * mm});
            skLineSegment(sketch, "E31.0.18.0", {"start": v(-31.1, 23.92) * mm, "end": v(-30.6, 23.92) * mm});
            skLineSegment(sketch, "E31.3.18.0", {"start": v(-31.09, 25.92) * mm, "end": v(-31.1, 23.92) * mm, "construction": true});
            skLineSegment(sketch, "E31.6.18.0", {"start": v(-30.6, 24.42) * mm, "end": v(-30.6, 23.92) * mm});
            skLineSegment(sketch, "E31.9.18.0", {"start": v(-31.1, 24.42) * mm, "end": v(-30.6, 24.42) * mm});
            skLineSegment(sketch, "E31.0.19.0", {"start": v(-33.6, 23.92) * mm, "end": v(-33.1, 23.92) * mm});
            skLineSegment(sketch, "E31.3.19.0", {"start": v(-33.59, 25.92) * mm, "end": v(-33.6, 23.92) * mm, "construction": true});
            skLineSegment(sketch, "E31.6.19.0", {"start": v(-33.1, 24.42) * mm, "end": v(-33.1, 23.92) * mm});
            skLineSegment(sketch, "E31.9.19.0", {"start": v(-33.6, 24.42) * mm, "end": v(-33.1, 24.42) * mm});
            skLineSegment(sketch, "E32", {"start": v(11.4, 24.43) * mm, "end": v(11.4, 23.93) * mm});
            skLineSegment(sketch, "E33", {"start": v(8.9, 24.43) * mm, "end": v(8.9, 23.93) * mm});
            skLineSegment(sketch, "E34", {"start": v(6.4, 23.93) * mm, "end": v(6.4, 24.43) * mm});
            skLineSegment(sketch, "E35", {"start": v(3.9, 24.43) * mm, "end": v(3.9, 23.93) * mm});
            skLineSegment(sketch, "E36", {"start": v(1.4, 24.43) * mm, "end": v(1.4, 23.93) * mm});
            skLineSegment(sketch, "E37", {"start": v(-1.1, 24.43) * mm, "end": v(-1.1, 23.93) * mm});
            skLineSegment(sketch, "E38", {"start": v(-3.6, 24.43) * mm, "end": v(-3.6, 23.93) * mm});
            skLineSegment(sketch, "E39", {"start": v(-6.1, 24.43) * mm, "end": v(-6.1, 23.93) * mm});
            skLineSegment(sketch, "E40", {"start": v(-8.6, 24.43) * mm, "end": v(-8.6, 23.93) * mm});
            skLineSegment(sketch, "E41", {"start": v(-11.1, 24.43) * mm, "end": v(-11.1, 23.93) * mm});
            skLineSegment(sketch, "E42", {"start": v(-13.6, 24.43) * mm, "end": v(-13.6, 23.93) * mm});
            skLineSegment(sketch, "E43", {"start": v(-16.1, 24.43) * mm, "end": v(-16.1, 23.93) * mm});
            skLineSegment(sketch, "E44", {"start": v(-18.6, 24.43) * mm, "end": v(-18.6, 23.93) * mm});
            skLineSegment(sketch, "E45", {"start": v(-21.1, 24.42) * mm, "end": v(-21.1, 23.92) * mm});
            skLineSegment(sketch, "E46", {"start": v(-23.6, 24.42) * mm, "end": v(-23.6, 23.92) * mm});
            skLineSegment(sketch, "E47", {"start": v(-26.1, 24.42) * mm, "end": v(-26.1, 23.92) * mm});
            skLineSegment(sketch, "E48", {"start": v(-28.6, 24.42) * mm, "end": v(-28.6, 23.92) * mm});
            skLineSegment(sketch, "E49", {"start": v(-31.1, 24.42) * mm, "end": v(-31.1, 23.92) * mm});
            skLineSegment(sketch, "E50", {"start": v(-33.6, 24.42) * mm, "end": v(-33.6, 23.92) * mm});
            skSolve(sketch);
        }
        {
            var Q0;
            Q0 = qSketchRegion(id + "F26", true);
            var Q1;
            Q1 = qConstructionFilter(qBodyType(qCreatedBy(id + "F26" ,EDGE), BodyType.WIRE), ConstructionObject.NO);
            extrude(context, id + "F27", {"entities" : qUnion([Q0]), "surfaceEntities" : qUnion([Q1]), "depth" : 6 * mm});
        }
        {
            var Q0;
            Q0 = qSketchRegion(id + "F26", true);
            extrude(context, id + "F28", {"entities" : qUnion([Q0]), "operationType" : NewBodyOperationType.ADD, "depth" : -6 * mm});
        }
        {
            var Q0;
            Q0=makeQuery(id+"F1.opExtrude","CAP_FACE",FACE,{"disambiguationData":[OSD([sQuery(id+"F0.wireOp",EDGE,"E0.bottom"),sQuery(id+"F0.wireOp",EDGE,"E0.top"),sQuery(id+"F0.wireOp",EDGE,"E0.left"),sQuery(id+"F0.wireOp",EDGE,"E0.right"),sQuery(id+"F0.wireOp",EDGE,"E2"),sQuery(id+"F0.wireOp",EDGE,"E3"),sQuery(id+"F0.wireOp",EDGE,"E4"),sQuery(id+"F0.wireOp",EDGE,"E5"),sQuery(id+"F0.wireOp",EDGE,"E6.bottom"),sQuery(id+"F0.wireOp",EDGE,"E7.filletArc"),sQuery(id+"F0.wireOp",EDGE,"E8.filletArc"),sQuery(id+"F0.wireOp",EDGE,"E9.filletArc"),sQuery(id+"F0.wireOp",EDGE,"E10.filletArc")])],"isStart":false});
            var sketch = newSketch(context, id + "F29", { "sketchPlane" : qUnion([Q0])});
            skLineSegment(sketch, "E51.bottom", {"start": v(4.16, 13.44) * mm, "end": v(17.16, 13.44) * mm});
            skLineSegment(sketch, "E51.top", {"start": v(4.16, 6.44) * mm, "end": v(17.16, 6.44) * mm});
            skLineSegment(sketch, "E51.left", {"start": v(4.16, 13.44) * mm, "end": v(4.16, 6.44) * mm});
            skLineSegment(sketch, "E51.right", {"start": v(17.16, 13.44) * mm, "end": v(17.16, 6.44) * mm});
            skSolve(sketch);
        }
        {
            var Q0;
            Q0 = qSketchRegion(id + "F29", true);
            extrude(context, id + "F30", {"entities" : qUnion([Q0]), "operationType" : NewBodyOperationType.ADD, "depth" : 0.5 * mm});
        }
        {
            var Q0;
            Q0=makeQuery(id+"F1.opExtrude","CAP_FACE",FACE,{"disambiguationData":[OSD([sQuery(id+"F0.wireOp",EDGE,"E0.bottom"),sQuery(id+"F0.wireOp",EDGE,"E0.top"),sQuery(id+"F0.wireOp",EDGE,"E0.left"),sQuery(id+"F0.wireOp",EDGE,"E0.right"),sQuery(id+"F0.wireOp",EDGE,"E2"),sQuery(id+"F0.wireOp",EDGE,"E3"),sQuery(id+"F0.wireOp",EDGE,"E4"),sQuery(id+"F0.wireOp",EDGE,"E5"),sQuery(id+"F0.wireOp",EDGE,"E6.bottom"),sQuery(id+"F0.wireOp",EDGE,"E7.filletArc"),sQuery(id+"F0.wireOp",EDGE,"E8.filletArc"),sQuery(id+"F0.wireOp",EDGE,"E9.filletArc"),sQuery(id+"F0.wireOp",EDGE,"E10.filletArc")])],"isStart":false});
            var sketch = newSketch(context, id + "F31", { "sketchPlane" : qUnion([Q0])});
            skLineSegment(sketch, "E52.bottom", {"start": v(19.16, 21.44) * mm, "end": v(23.16, 21.44) * mm});
            skLineSegment(sketch, "E52.top", {"start": v(19.16, 17.44) * mm, "end": v(23.16, 17.44) * mm});
            skLineSegment(sketch, "E52.left", {"start": v(19.16, 21.44) * mm, "end": v(19.16, 17.44) * mm});
            skLineSegment(sketch, "E52.right", {"start": v(23.16, 21.44) * mm, "end": v(23.16, 17.44) * mm});
            skLineSegment(sketch, "E53.bottom", {"start": v(-22.84, 18.44) * mm, "end": v(-18.84, 18.44) * mm});
            skLineSegment(sketch, "E53.top", {"start": v(-22.84, 14.44) * mm, "end": v(-18.84, 14.44) * mm});
            skLineSegment(sketch, "E53.left", {"start": v(-22.84, 18.44) * mm, "end": v(-22.84, 14.44) * mm});
            skLineSegment(sketch, "E53.right", {"start": v(-18.84, 18.44) * mm, "end": v(-18.84, 14.44) * mm});
            skLineSegment(sketch, "E54.bottom", {"start": v(-13.84, -2.56) * mm, "end": v(-9.84, -2.56) * mm});
            skLineSegment(sketch, "E54.top", {"start": v(-13.84, -6.56) * mm, "end": v(-9.84, -6.56) * mm});
            skLineSegment(sketch, "E54.left", {"start": v(-13.84, -2.56) * mm, "end": v(-13.84, -6.56) * mm});
            skLineSegment(sketch, "E54.right", {"start": v(-9.84, -2.56) * mm, "end": v(-9.84, -6.56) * mm});
            skSolve(sketch);
        }
        {
            var Q0;
            Q0 = qSketchRegion(id + "F31", true);
            extrude(context, id + "F32", {"entities" : qUnion([Q0]), "operationType" : NewBodyOperationType.ADD, "depth" : 1.5 * mm});
        }
        {
            var Q0;
            Q0=makeQuery(id+"F1.opExtrude","CAP_FACE",FACE,{"disambiguationData":[OSD([sQuery(id+"F0.wireOp",EDGE,"E0.bottom"),sQuery(id+"F0.wireOp",EDGE,"E0.top"),sQuery(id+"F0.wireOp",EDGE,"E0.left"),sQuery(id+"F0.wireOp",EDGE,"E0.right"),sQuery(id+"F0.wireOp",EDGE,"E2"),sQuery(id+"F0.wireOp",EDGE,"E3"),sQuery(id+"F0.wireOp",EDGE,"E4"),sQuery(id+"F0.wireOp",EDGE,"E5"),sQuery(id+"F0.wireOp",EDGE,"E6.bottom"),sQuery(id+"F0.wireOp",EDGE,"E7.filletArc"),sQuery(id+"F0.wireOp",EDGE,"E8.filletArc"),sQuery(id+"F0.wireOp",EDGE,"E9.filletArc"),sQuery(id+"F0.wireOp",EDGE,"E10.filletArc")])],"isStart":false});
            var sketch = newSketch(context, id + "F33", { "sketchPlane" : qUnion([Q0])});
            skLineSegment(sketch, "E55.bottom", {"start": v(0.16, 20.44) * mm, "end": v(1.16, 20.44) * mm});
            skLineSegment(sketch, "E55.top", {"start": v(0.16, 19.44) * mm, "end": v(1.16, 19.44) * mm});
            skLineSegment(sketch, "E55.left", {"start": v(0.16, 20.44) * mm, "end": v(0.16, 19.44) * mm});
            skLineSegment(sketch, "E55.right", {"start": v(1.16, 20.44) * mm, "end": v(1.16, 19.44) * mm});
            skLineSegment(sketch, "E56.bottom", {"start": v(5.16, 20.44) * mm, "end": v(6.16, 20.44) * mm});
            skLineSegment(sketch, "E56.top", {"start": v(5.16, 19.44) * mm, "end": v(6.16, 19.44) * mm});
            skLineSegment(sketch, "E56.left", {"start": v(5.16, 20.44) * mm, "end": v(5.16, 19.44) * mm});
            skLineSegment(sketch, "E56.right", {"start": v(6.16, 20.44) * mm, "end": v(6.16, 19.44) * mm});
            skSolve(sketch);
        }
        {
            var Q0;
            Q0 = qSketchRegion(id + "F33", true);
            extrude(context, id + "F34", {"entities" : qUnion([Q0]), "operationType" : NewBodyOperationType.ADD, "depth" : .5 * mm});
        }
        {
            var Q0;
            Q0=makeQuery(id+"F1.opExtrude","CAP_FACE",FACE,{"disambiguationData":[OSD([sQuery(id+"F0.wireOp",EDGE,"E0.bottom"),sQuery(id+"F0.wireOp",EDGE,"E0.top"),sQuery(id+"F0.wireOp",EDGE,"E0.left"),sQuery(id+"F0.wireOp",EDGE,"E0.right"),sQuery(id+"F0.wireOp",EDGE,"E2"),sQuery(id+"F0.wireOp",EDGE,"E3"),sQuery(id+"F0.wireOp",EDGE,"E4"),sQuery(id+"F0.wireOp",EDGE,"E5"),sQuery(id+"F0.wireOp",EDGE,"E6.bottom"),sQuery(id+"F0.wireOp",EDGE,"E7.filletArc"),sQuery(id+"F0.wireOp",EDGE,"E8.filletArc"),sQuery(id+"F0.wireOp",EDGE,"E9.filletArc"),sQuery(id+"F0.wireOp",EDGE,"E10.filletArc")])],"isStart":false});
            var sketch = newSketch(context, id + "F35", { "sketchPlane" : qUnion([Q0])});
            skLineSegment(sketch, "E57.bottom", {"start": v(-12.74, 19.44) * mm, "end": v(-2.84, 9.54) * mm});
            skLineSegment(sketch, "E57.top", {"start": v(-22.64, 9.54) * mm, "end": v(-12.74, -0.36) * mm});
            skLineSegment(sketch, "E57.left", {"start": v(-12.74, 19.44) * mm, "end": v(-22.64, 9.54) * mm});
            skLineSegment(sketch, "E57.right", {"start": v(-2.84, 9.54) * mm, "end": v(-12.74, -0.36) * mm});
            skSolve(sketch);
        }
        {
            var Q0;
            Q0 = qSketchRegion(id + "F35", true);
            extrude(context, id + "F36", {"entities" : qUnion([Q0]), "operationType" : NewBodyOperationType.ADD, "depth" : .5 * mm});
        }
        {
            var Q0;
            Q0 = qSketchRegion(id + "F18", true);
            extrude(context, id + "F37", {"entities" : qUnion([Q0]), "operationType" : NewBodyOperationType.ADD, "depth" : -6 * mm});
        }
        {
            var Q0;
            Q0=makeQuery(id+"F0.imprint","IMPRINT",FACE,{"disambiguationData":[TD([[makeQuery(id+"F0.imprint","IMPRINT",EDGE,{"derivedFrom":sQuery(id+"F0.wireOp",EDGE,"E0.bottom")}),-1.0]])]});
            var sketch = newSketch(context, id + "F38", { "sketchPlane" : qUnion([Q0])});
            skLineSegment(sketch, "E58.bottom", {"start": v(-8.34, -19.56) * mm, "end": v(8.16, -19.56) * mm});
            skLineSegment(sketch, "E58.top", {"start": v(-8.34, -13.56) * mm, "end": v(8.16, -13.56) * mm});
            skLineSegment(sketch, "E58.left", {"start": v(-8.34, -19.56) * mm, "end": v(-8.34, -13.56) * mm});
            skLineSegment(sketch, "E58.right", {"start": v(8.16, -19.56) * mm, "end": v(8.16, -13.56) * mm});
            skSolve(sketch);
        }
        {
            var Q0;
            Q0 = qSketchRegion(id + "F38", true);
            extrude(context, id + "F39", {"entities" : qUnion([Q0]), "operationType" : NewBodyOperationType.ADD, "depth" : -2 * mm});
        }
        {
            var Q0;
            Q0=makeQuery(id+"F0.imprint","IMPRINT",FACE,{"disambiguationData":[TD([[makeQuery(id+"F0.imprint","IMPRINT",EDGE,{"derivedFrom":sQuery(id+"F0.wireOp",EDGE,"E0.bottom")}),-1.0]])]});
            var sketch = newSketch(context, id + "F40", { "sketchPlane" : qUnion([Q0])});
            skLineSegment(sketch, "E59.bottom", {"start": v(-3.34, -8.56) * mm, "end": v(1.16, -8.56) * mm});
            skLineSegment(sketch, "E59.top", {"start": v(-3.34, -4.06) * mm, "end": v(1.16, -4.06) * mm});
            skLineSegment(sketch, "E59.left", {"start": v(-3.34, -8.56) * mm, "end": v(-3.34, -4.06) * mm});
            skLineSegment(sketch, "E59.right", {"start": v(1.16, -8.56) * mm, "end": v(1.16, -4.06) * mm});
            skSolve(sketch);
        }
        {
            var Q0;
            Q0 = qSketchRegion(id + "F40", true);
            extrude(context, id + "F41", {"entities" : qUnion([Q0]), "operationType" : NewBodyOperationType.ADD, "depth" : -2 * mm});
        }
        {
            var Q0;
            Q0=makeQuery(id+"F0.imprint","IMPRINT",FACE,{"disambiguationData":[TD([[makeQuery(id+"F0.imprint","IMPRINT",EDGE,{"derivedFrom":sQuery(id+"F0.wireOp",EDGE,"E0.bottom")}),-1.0]])]});
            var sketch = newSketch(context, id + "F42", { "sketchPlane" : qUnion([Q0])});
            skLineSegment(sketch, "E60.bottom", {"start": v(3.66, 4.94) * mm, "end": v(17.16, 4.94) * mm});
            skLineSegment(sketch, "E60.top", {"start": v(3.66, 12.44) * mm, "end": v(17.16, 12.44) * mm});
            skLineSegment(sketch, "E60.left", {"start": v(3.66, 4.94) * mm, "end": v(3.66, 12.44) * mm});
            skLineSegment(sketch, "E60.right", {"start": v(17.16, 4.94) * mm, "end": v(17.16, 12.44) * mm});
            skSolve(sketch);
        }
        {
            var Q0;
            Q0 = qSketchRegion(id + "F42", true);
            extrude(context, id + "F43", {"entities" : qUnion([Q0]), "operationType" : NewBodyOperationType.ADD, "depth" : -0.5 * mm});
        }
        {
            var Q0;
            Q0=makeQuery(id+"F0.imprint","IMPRINT",FACE,{"disambiguationData":[TD([[makeQuery(id+"F0.imprint","IMPRINT",EDGE,{"derivedFrom":sQuery(id+"F0.wireOp",EDGE,"E0.bottom")}),-1.0]])]});
            var sketch = newSketch(context, id + "F44", { "sketchPlane" : qUnion([Q0])});
            skLineSegment(sketch, "E61.bottom", {"start": v(14.66, -5.56) * mm, "end": v(23.66, -5.56) * mm});
            skLineSegment(sketch, "E61.top", {"start": v(14.66, 0.44) * mm, "end": v(23.66, 0.44) * mm});
            skLineSegment(sketch, "E61.left", {"start": v(14.66, -5.56) * mm, "end": v(14.66, 0.44) * mm});
            skLineSegment(sketch, "E61.right", {"start": v(23.66, -5.56) * mm, "end": v(23.66, 0.44) * mm});
            skSolve(sketch);
        }
        {
            var Q0;
            Q0 = qSketchRegion(id + "F44", true);
            extrude(context, id + "F45", {"entities" : qUnion([Q0]), "operationType" : NewBodyOperationType.ADD, "depth" : -2 * mm});
        }
        {
            var Q0;
            Q0=makeQuery(id+"F0.imprint","IMPRINT",FACE,{"disambiguationData":[TD([[makeQuery(id+"F0.imprint","IMPRINT",EDGE,{"derivedFrom":sQuery(id+"F0.wireOp",EDGE,"E0.bottom")}),-1.0]])]});
            var sketch = newSketch(context, id + "F46", { "sketchPlane" : qUnion([Q0])});
            skLineSegment(sketch, "E62.bottom", {"start": v(-36.84, 11.44) * mm, "end": v(-35.84, 11.44) * mm});
            skLineSegment(sketch, "E62.top", {"start": v(-36.84, 12.44) * mm, "end": v(-35.84, 12.44) * mm});
            skLineSegment(sketch, "E62.left", {"start": v(-36.84, 11.44) * mm, "end": v(-36.84, 12.44) * mm});
            skLineSegment(sketch, "E62.right", {"start": v(-35.84, 11.44) * mm, "end": v(-35.84, 12.44) * mm});
            skLineSegment(sketch, "E63.bottom", {"start": v(-29.84, 11.44) * mm, "end": v(-28.84, 11.44) * mm});
            skLineSegment(sketch, "E63.top", {"start": v(-29.84, 12.44) * mm, "end": v(-28.84, 12.44) * mm});
            skLineSegment(sketch, "E63.left", {"start": v(-29.84, 11.44) * mm, "end": v(-29.84, 12.44) * mm});
            skLineSegment(sketch, "E63.right", {"start": v(-28.84, 11.44) * mm, "end": v(-28.84, 12.44) * mm});
            skLineSegment(sketch, "E64.bottom", {"start": v(-36.84, 17.94) * mm, "end": v(-35.84, 17.94) * mm});
            skLineSegment(sketch, "E64.top", {"start": v(-36.84, 18.94) * mm, "end": v(-35.84, 18.94) * mm});
            skLineSegment(sketch, "E64.left", {"start": v(-36.84, 17.94) * mm, "end": v(-36.84, 18.94) * mm});
            skLineSegment(sketch, "E64.right", {"start": v(-35.84, 17.94) * mm, "end": v(-35.84, 18.94) * mm});
            skLineSegment(sketch, "E65.bottom", {"start": v(-29.84, 17.94) * mm, "end": v(-28.84, 17.94) * mm});
            skLineSegment(sketch, "E65.top", {"start": v(-29.84, 18.94) * mm, "end": v(-28.84, 18.94) * mm});
            skLineSegment(sketch, "E65.left", {"start": v(-29.84, 17.94) * mm, "end": v(-29.84, 18.94) * mm});
            skLineSegment(sketch, "E65.right", {"start": v(-28.84, 17.94) * mm, "end": v(-28.84, 18.94) * mm});
            skLineSegment(sketch, "E66.bottom", {"start": v(-34.84, 9.44) * mm, "end": v(-33.84, 9.44) * mm});
            skLineSegment(sketch, "E66.top", {"start": v(-34.84, 10.44) * mm, "end": v(-33.84, 10.44) * mm});
            skLineSegment(sketch, "E66.left", {"start": v(-34.84, 9.44) * mm, "end": v(-34.84, 10.44) * mm});
            skLineSegment(sketch, "E66.right", {"start": v(-33.84, 9.44) * mm, "end": v(-33.84, 10.44) * mm});
            skLineSegment(sketch, "E67.bottom", {"start": v(-34.84, -1.06) * mm, "end": v(-33.84, -1.06) * mm});
            skLineSegment(sketch, "E67.top", {"start": v(-34.84, -0.06) * mm, "end": v(-33.84, -0.06) * mm});
            skLineSegment(sketch, "E67.left", {"start": v(-34.84, -1.06) * mm, "end": v(-34.84, -0.06) * mm});
            skLineSegment(sketch, "E67.right", {"start": v(-33.84, -1.06) * mm, "end": v(-33.84, -0.06) * mm});
            skLineSegment(sketch, "E68.bottom", {"start": v(-41.34, -5.06) * mm, "end": v(-40.84, -5.06) * mm});
            skLineSegment(sketch, "E68.top", {"start": v(-41.34, -4.56) * mm, "end": v(-40.84, -4.56) * mm});
            skLineSegment(sketch, "E68.left", {"start": v(-41.34, -5.06) * mm, "end": v(-41.34, -4.56) * mm});
            skLineSegment(sketch, "E68.right", {"start": v(-40.84, -5.06) * mm, "end": v(-40.84, -4.56) * mm});
            skLineSegment(sketch, "E69.bottom", {"start": v(-41.34, -2.56) * mm, "end": v(-40.84, -2.56) * mm});
            skLineSegment(sketch, "E69.top", {"start": v(-41.34, -2.06) * mm, "end": v(-40.84, -2.06) * mm});
            skLineSegment(sketch, "E69.left", {"start": v(-41.34, -2.56) * mm, "end": v(-41.34, -2.06) * mm});
            skLineSegment(sketch, "E69.right", {"start": v(-40.84, -2.56) * mm, "end": v(-40.84, -2.06) * mm});
            skLineSegment(sketch, "E70.bottom", {"start": v(-30.84, -1.66) * mm, "end": v(-30.34, -1.66) * mm});
            skLineSegment(sketch, "E70.top", {"start": v(-30.84, -1.16) * mm, "end": v(-30.34, -1.16) * mm});
            skLineSegment(sketch, "E70.left", {"start": v(-30.84, -1.66) * mm, "end": v(-30.84, -1.16) * mm});
            skLineSegment(sketch, "E70.right", {"start": v(-30.34, -1.66) * mm, "end": v(-30.34, -1.16) * mm});
            skLineSegment(sketch, "E71.bottom", {"start": v(-28.64, -2.86) * mm, "end": v(-28.14, -2.86) * mm});
            skLineSegment(sketch, "E71.top", {"start": v(-28.64, -2.36) * mm, "end": v(-28.14, -2.36) * mm});
            skLineSegment(sketch, "E71.left", {"start": v(-28.64, -2.86) * mm, "end": v(-28.64, -2.36) * mm});
            skLineSegment(sketch, "E71.right", {"start": v(-28.14, -2.86) * mm, "end": v(-28.14, -2.36) * mm});
            skLineSegment(sketch, "E72.bottom", {"start": v(-30.84, 1.04) * mm, "end": v(-30.34, 1.04) * mm});
            skLineSegment(sketch, "E72.top", {"start": v(-30.84, 1.54) * mm, "end": v(-30.34, 1.54) * mm});
            skLineSegment(sketch, "E72.left", {"start": v(-30.84, 1.04) * mm, "end": v(-30.84, 1.54) * mm});
            skLineSegment(sketch, "E72.right", {"start": v(-30.34, 1.04) * mm, "end": v(-30.34, 1.54) * mm});
            skLineSegment(sketch, "E73.bottom", {"start": v(-28.64, -0.16) * mm, "end": v(-28.14, -0.16) * mm});
            skLineSegment(sketch, "E73.top", {"start": v(-28.64, 0.34) * mm, "end": v(-28.14, 0.34) * mm});
            skLineSegment(sketch, "E73.left", {"start": v(-28.64, -0.16) * mm, "end": v(-28.64, 0.34) * mm});
            skLineSegment(sketch, "E73.right", {"start": v(-28.14, -0.16) * mm, "end": v(-28.14, 0.34) * mm});
            skLineSegment(sketch, "E74.bottom", {"start": v(-30.84, 3.74) * mm, "end": v(-30.34, 3.74) * mm});
            skLineSegment(sketch, "E74.top", {"start": v(-30.84, 4.24) * mm, "end": v(-30.34, 4.24) * mm});
            skLineSegment(sketch, "E74.left", {"start": v(-30.84, 3.74) * mm, "end": v(-30.84, 4.24) * mm});
            skLineSegment(sketch, "E74.right", {"start": v(-30.34, 3.74) * mm, "end": v(-30.34, 4.24) * mm});
            skLineSegment(sketch, "E75.bottom", {"start": v(-28.64, 2.54) * mm, "end": v(-28.14, 2.54) * mm});
            skLineSegment(sketch, "E75.top", {"start": v(-28.64, 3.04) * mm, "end": v(-28.14, 3.04) * mm});
            skLineSegment(sketch, "E75.left", {"start": v(-28.64, 2.54) * mm, "end": v(-28.64, 3.04) * mm});
            skLineSegment(sketch, "E75.right", {"start": v(-28.14, 2.54) * mm, "end": v(-28.14, 3.04) * mm});
            skLineSegment(sketch, "E76.bottom", {"start": v(-30.84, 6.44) * mm, "end": v(-30.34, 6.44) * mm});
            skLineSegment(sketch, "E76.top", {"start": v(-30.84, 6.94) * mm, "end": v(-30.34, 6.94) * mm});
            skLineSegment(sketch, "E76.left", {"start": v(-30.84, 6.44) * mm, "end": v(-30.84, 6.94) * mm});
            skLineSegment(sketch, "E76.right", {"start": v(-30.34, 6.44) * mm, "end": v(-30.34, 6.94) * mm});
            skLineSegment(sketch, "E77.bottom", {"start": v(-28.64, 5.24) * mm, "end": v(-28.14, 5.24) * mm});
            skLineSegment(sketch, "E77.top", {"start": v(-28.64, 5.74) * mm, "end": v(-28.14, 5.74) * mm});
            skLineSegment(sketch, "E77.left", {"start": v(-28.64, 5.24) * mm, "end": v(-28.64, 5.74) * mm});
            skLineSegment(sketch, "E77.right", {"start": v(-28.14, 5.24) * mm, "end": v(-28.14, 5.74) * mm});
            skLineSegment(sketch, "E78.bottom", {"start": v(-41.34, 8.94) * mm, "end": v(-40.84, 8.94) * mm});
            skLineSegment(sketch, "E78.top", {"start": v(-41.34, 9.44) * mm, "end": v(-40.84, 9.44) * mm});
            skLineSegment(sketch, "E78.left", {"start": v(-41.34, 8.94) * mm, "end": v(-41.34, 9.44) * mm});
            skLineSegment(sketch, "E78.right", {"start": v(-40.84, 8.94) * mm, "end": v(-40.84, 9.44) * mm});
            skLineSegment(sketch, "E79.bottom", {"start": v(-41.34, 6.44) * mm, "end": v(-40.84, 6.44) * mm});
            skLineSegment(sketch, "E79.top", {"start": v(-41.34, 6.94) * mm, "end": v(-40.84, 6.94) * mm});
            skLineSegment(sketch, "E79.left", {"start": v(-41.34, 6.44) * mm, "end": v(-41.34, 6.94) * mm});
            skLineSegment(sketch, "E79.right", {"start": v(-40.84, 6.44) * mm, "end": v(-40.84, 6.94) * mm});
            skSolve(sketch);
        }
        {
            var Q0;
            Q0 = qSketchRegion(id + "F46", true);
            extrude(context, id + "F47", {"entities" : qUnion([Q0]), "operationType" : NewBodyOperationType.ADD, "depth" : -3 * mm});
        }
        {
            var Q0;
            Q0=makeQuery(id+"F0.imprint","IMPRINT",FACE,{"disambiguationData":[TD([[makeQuery(id+"F0.imprint","IMPRINT",EDGE,{"derivedFrom":sQuery(id+"F0.wireOp",EDGE,"E0.bottom")}),-1.0]])]});
            var sketch = newSketch(context, id + "F48", { "sketchPlane" : qUnion([Q0])});
            skLineSegment(sketch, "E80.bottom", {"start": v(-38.84, -5.06) * mm, "end": v(-35.84, -5.06) * mm});
            skLineSegment(sketch, "E80.top", {"start": v(-38.84, -2.06) * mm, "end": v(-35.84, -2.06) * mm});
            skLineSegment(sketch, "E80.left", {"start": v(-38.84, -5.06) * mm, "end": v(-38.84, -2.06) * mm});
            skLineSegment(sketch, "E80.right", {"start": v(-35.84, -5.06) * mm, "end": v(-35.84, -2.06) * mm});
            skLineSegment(sketch, "E81.bottom", {"start": v(-38.84, 6.44) * mm, "end": v(-35.84, 6.44) * mm});
            skLineSegment(sketch, "E81.top", {"start": v(-38.84, 9.44) * mm, "end": v(-35.84, 9.44) * mm});
            skLineSegment(sketch, "E81.left", {"start": v(-38.84, 6.44) * mm, "end": v(-38.84, 9.44) * mm});
            skLineSegment(sketch, "E81.right", {"start": v(-35.84, 6.44) * mm, "end": v(-35.84, 9.44) * mm});
            skLineSegment(sketch, "E82.bottom", {"start": v(-25.84, -12.56) * mm, "end": v(-25.34, -12.56) * mm});
            skLineSegment(sketch, "E82.top", {"start": v(-25.84, -10.56) * mm, "end": v(-25.34, -10.56) * mm});
            skLineSegment(sketch, "E82.left", {"start": v(-25.84, -12.56) * mm, "end": v(-25.84, -10.56) * mm});
            skLineSegment(sketch, "E82.right", {"start": v(-25.34, -12.56) * mm, "end": v(-25.34, -10.56) * mm});
            skLineSegment(sketch, "E83.bottom", {"start": v(-11.34, -12.56) * mm, "end": v(-10.84, -12.56) * mm});
            skLineSegment(sketch, "E83.top", {"start": v(-11.34, -10.56) * mm, "end": v(-10.84, -10.56) * mm});
            skLineSegment(sketch, "E83.left", {"start": v(-11.34, -12.56) * mm, "end": v(-11.34, -10.56) * mm});
            skLineSegment(sketch, "E83.right", {"start": v(-10.84, -12.56) * mm, "end": v(-10.84, -10.56) * mm});
            skLineSegment(sketch, "E84.bottom", {"start": v(-25.84, -17.56) * mm, "end": v(-25.34, -17.56) * mm});
            skLineSegment(sketch, "E84.top", {"start": v(-25.84, -17.06) * mm, "end": v(-25.34, -17.06) * mm});
            skLineSegment(sketch, "E84.left", {"start": v(-25.84, -17.56) * mm, "end": v(-25.84, -17.06) * mm});
            skLineSegment(sketch, "E84.right", {"start": v(-25.34, -17.56) * mm, "end": v(-25.34, -17.06) * mm});
            skLineSegment(sketch, "E85.bottom", {"start": v(-11.34, -17.56) * mm, "end": v(-10.84, -17.56) * mm});
            skLineSegment(sketch, "E85.top", {"start": v(-11.34, -17.06) * mm, "end": v(-10.84, -17.06) * mm});
            skLineSegment(sketch, "E85.left", {"start": v(-11.34, -17.56) * mm, "end": v(-11.34, -17.06) * mm});
            skLineSegment(sketch, "E85.right", {"start": v(-10.84, -17.56) * mm, "end": v(-10.84, -17.06) * mm});
            skLineSegment(sketch, "E86.bottom", {"start": v(11.16, -13.56) * mm, "end": v(12.16, -13.56) * mm});
            skLineSegment(sketch, "E86.top", {"start": v(11.16, -12.56) * mm, "end": v(12.16, -12.56) * mm});
            skLineSegment(sketch, "E86.left", {"start": v(11.16, -13.56) * mm, "end": v(11.16, -12.56) * mm});
            skLineSegment(sketch, "E86.right", {"start": v(12.16, -13.56) * mm, "end": v(12.16, -12.56) * mm});
            skLineSegment(sketch, "E87.bottom", {"start": v(12.66, -10.56) * mm, "end": v(13.66, -10.56) * mm});
            skLineSegment(sketch, "E87.top", {"start": v(12.66, -9.56) * mm, "end": v(13.66, -9.56) * mm});
            skLineSegment(sketch, "E87.left", {"start": v(12.66, -10.56) * mm, "end": v(12.66, -9.56) * mm});
            skLineSegment(sketch, "E87.right", {"start": v(13.66, -10.56) * mm, "end": v(13.66, -9.56) * mm});
            skLineSegment(sketch, "E88.bottom", {"start": v(16.16, -11.56) * mm, "end": v(17.16, -11.56) * mm});
            skLineSegment(sketch, "E88.top", {"start": v(16.16, -10.56) * mm, "end": v(17.16, -10.56) * mm});
            skLineSegment(sketch, "E88.left", {"start": v(16.16, -11.56) * mm, "end": v(16.16, -10.56) * mm});
            skLineSegment(sketch, "E88.right", {"start": v(17.16, -11.56) * mm, "end": v(17.16, -10.56) * mm});
            skSolve(sketch);
        }
        {
            var Q0;
            Q0 = qSketchRegion(id + "F48", true);
            extrude(context, id + "F49", {"entities" : qUnion([Q0]), "operationType" : NewBodyOperationType.ADD, "depth" : -2 * mm});
        }
    });
